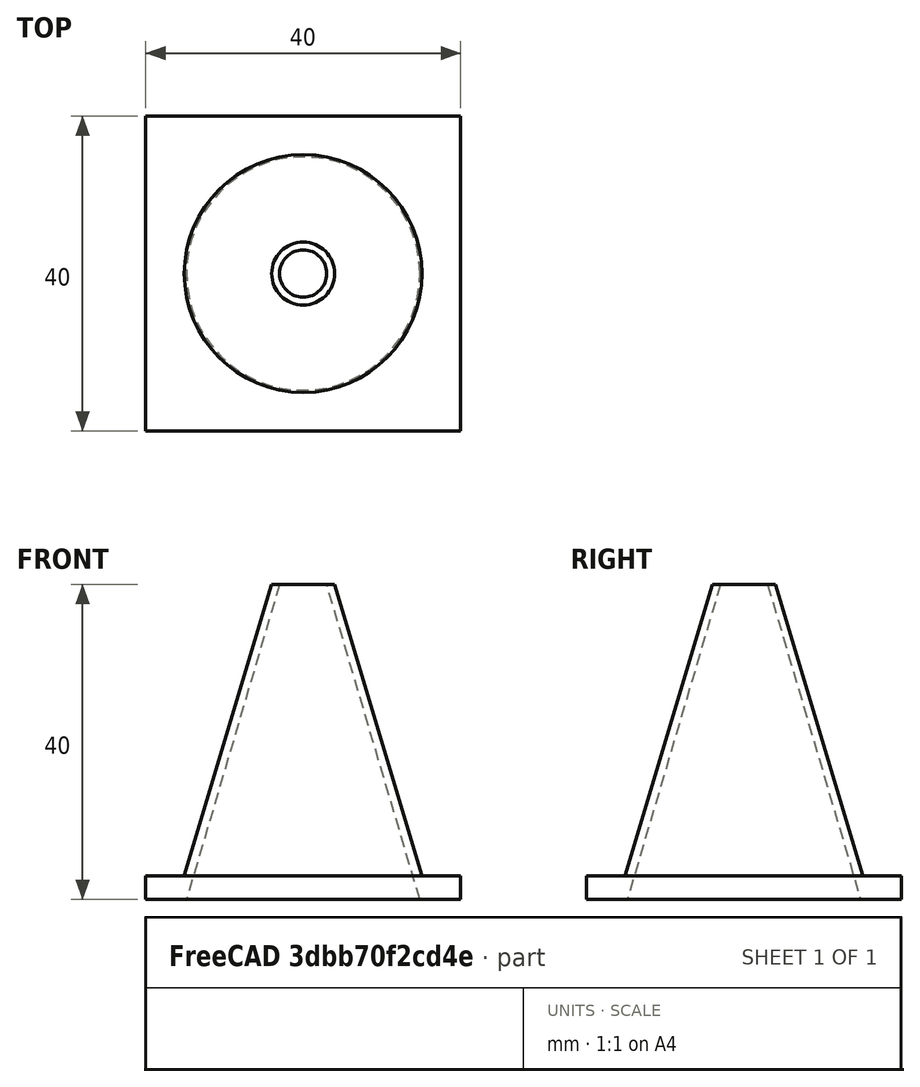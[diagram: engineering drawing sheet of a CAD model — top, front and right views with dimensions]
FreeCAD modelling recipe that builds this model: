
FCSTD DOCUMENT  (FreeCAD 0.18R16146 (Git))
Label: conotrafico_dani
License: All rights reserved
LicenseURL: http://en.wikipedia.org/wiki/All_rights_reserved
objects: Part::Cone×2, Part::Box×1, Part::MultiFuse×1, Part::Cut×1
note: 5 computed .brp shape members not serialized (recipe doc carries the construction recipe); baked Part::Feature solids carry a one-line shape summary decoded from their .brp

FEATURE [Part::Cone] Cone  label="Cono"
  Angle = 360
  AttacherType = Attacher::AttachEngine3D
  Height = 40
  Radius1 = 16
  Radius2 = 4
FEATURE [Part::Box] Box  label="Cubo"
  AttacherType = Attacher::AttachEngine3D
  Height = 3
  Length = 40
  Placement = pos=(-20,-20,0) rot=(0,0,1;0rad)
  Width = 40
FEATURE [Part::Cone] Cone001  label="Cono"
  Angle = 360
  AttacherType = Attacher::AttachEngine3D
  Height = 44
  Placement = pos=(0,0,-4) rot=(0,0,1;0rad)
  Radius1 = 16
  Radius2 = 3
FEATURE [Part::MultiFuse] Fusion
  Refine = true
  Shapes = -> [Box,Cone]
FEATURE [Part::Cut] Cut  label="cono"
  Base = -> Fusion
  Refine = true
  Tool = -> Cone001
